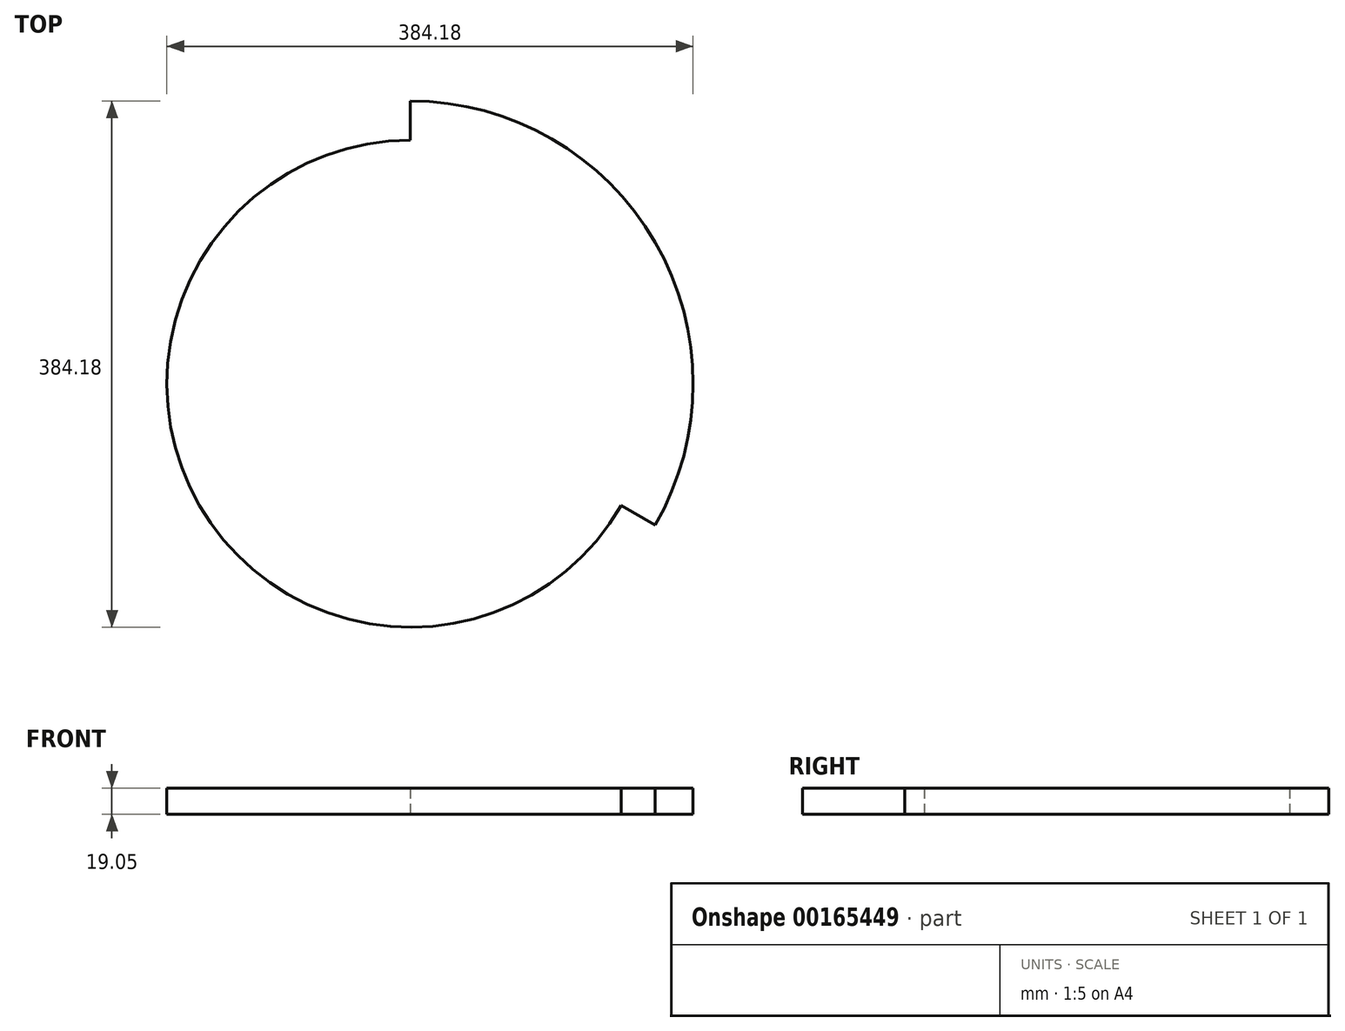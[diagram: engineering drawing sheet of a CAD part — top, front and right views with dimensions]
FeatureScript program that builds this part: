
annotation { "Feature Type Name" : "Feature", "Feature Type Description" : "" }
export const myFeature = defineFeature(function(context is Context, id is Id, definition is map)
    precondition{}
    {
        {
            var Q0;
            Q0=qCreatedBy(makeId("Top.planeOp"),FACE);
            var sketch = newSketch(context, id + "F0", { "sketchPlane" : qUnion([Q0])});
            skArc(sketch, "E0", {"start": v(0, 177.8) * mm, "mid": v(-153.98, -88.9) * mm, "end": v(153.98, -88.9) * mm});
            skCircle(sketch, "E1.0", {"center": v(0, 0) * mm, "radius": 206.38 * mm});
            skLineSegment(sketch, "E2", {"start": v(153.98, -88.9) * mm, "end": v(178.73, -103.19) * mm});
            skPoint(sketch, "E3.orphan", {"position": v(0, 206.38) * mm});
            skLineSegment(sketch, "E4", {"start": v(0, 206.38) * mm, "end": v(0, 177.8) * mm});
            skSolve(sketch);
        }
        {
            var Q0;
            Q0=makeQuery(id+"F0.imprint","IMPRINT",FACE,{"disambiguationData":[TD([[makeQuery(id+"F0.imprint","IMPRINT",EDGE,{"derivedFrom":sQuery(id+"F0.wireOp",EDGE,"E0")}),1.0]])]});
            extrude(context, id + "F1", {"entities" : qUnion([Q0]), "depth" : 19.05 * mm});
        }
    });
